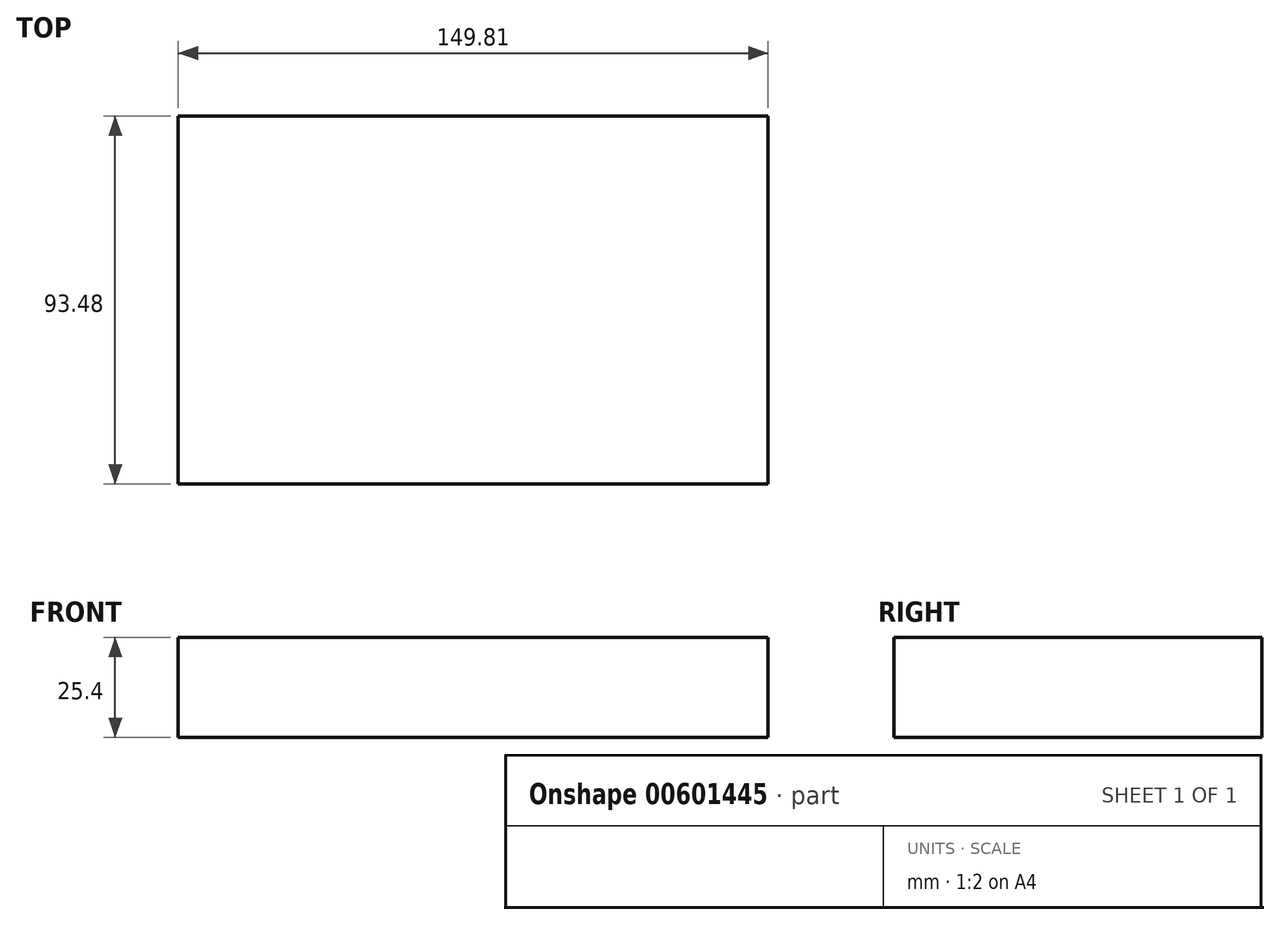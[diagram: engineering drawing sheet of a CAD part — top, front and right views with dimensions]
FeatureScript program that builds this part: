
annotation { "Feature Type Name" : "Feature", "Feature Type Description" : "" }
export const myFeature = defineFeature(function(context is Context, id is Id, definition is map)
    precondition{}
    {
        {
            var Q0;
            Q0=qCreatedBy(makeId("Top.planeOp"),FACE);
            var sketch = newSketch(context, id + "F0", { "sketchPlane" : qUnion([Q0])});
            skLineSegment(sketch, "E0.bottom", {"start": v(-49.45, 46.53) * mm, "end": v(100.36, 46.53) * mm});
            skLineSegment(sketch, "E0.top", {"start": v(-49.45, -46.95) * mm, "end": v(100.36, -46.95) * mm});
            skLineSegment(sketch, "E0.left", {"start": v(-49.45, 46.53) * mm, "end": v(-49.45, -46.95) * mm});
            skLineSegment(sketch, "E0.right", {"start": v(100.36, 46.53) * mm, "end": v(100.36, -46.95) * mm});
            skSolve(sketch);
        }
        {
            var Q0;
            Q0 = qSketchRegion(id + "F0", true);
            extrude(context, id + "F1", {"entities" : qUnion([Q0]), "depth" : 25.4 * mm, "offsetDistance" : 25.4 * mm});
        }
    });
